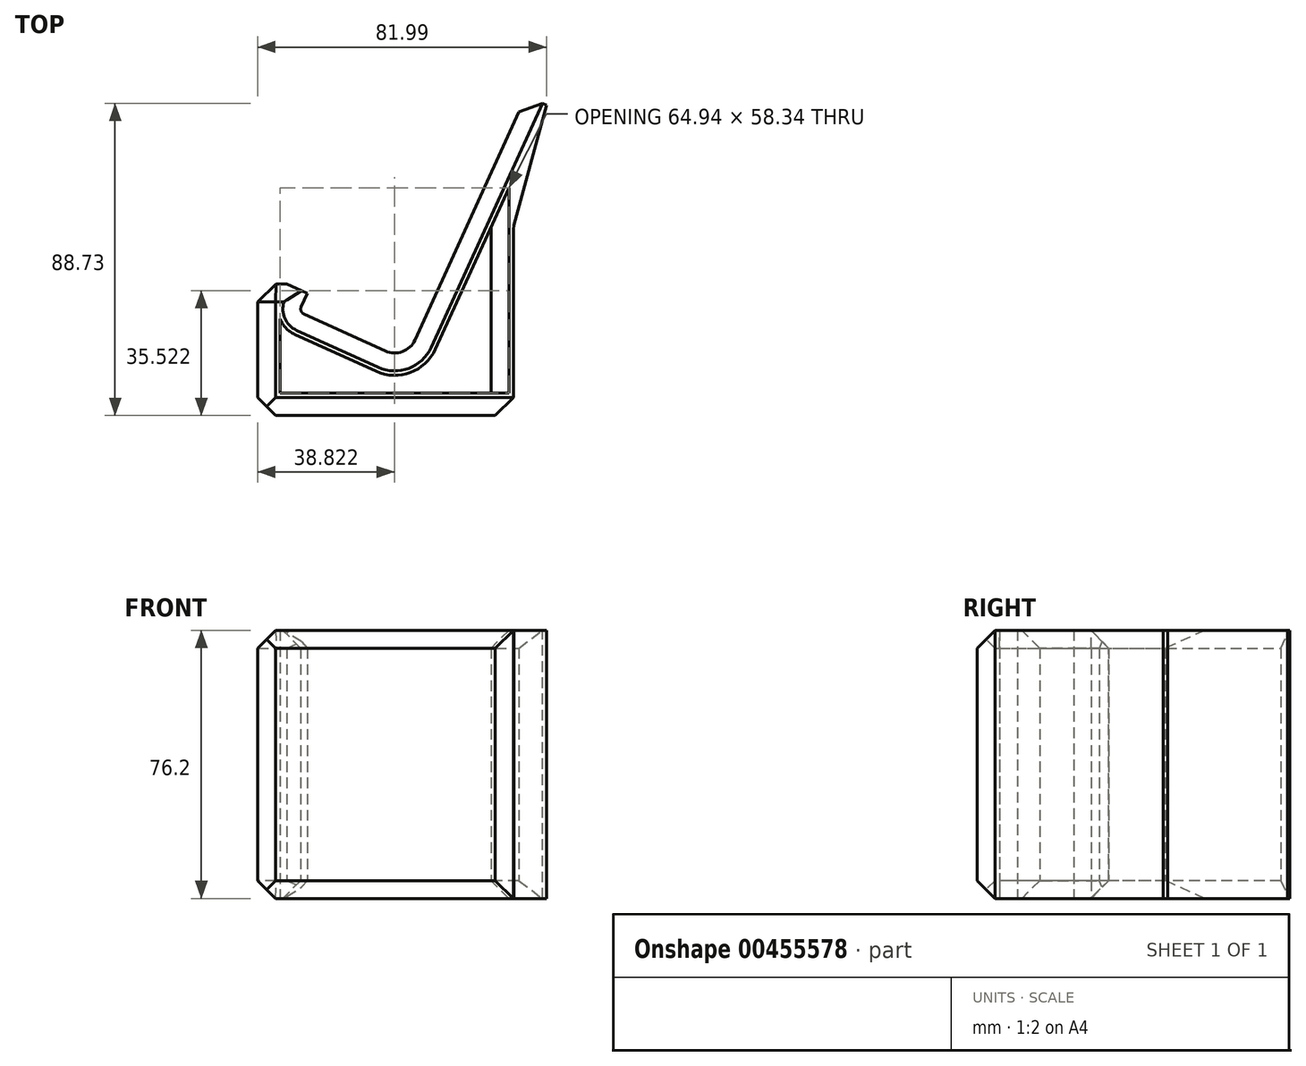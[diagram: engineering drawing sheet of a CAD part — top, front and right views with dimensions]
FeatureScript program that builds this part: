
annotation { "Feature Type Name" : "Feature", "Feature Type Description" : "" }
export const myFeature = defineFeature(function(context is Context, id is Id, definition is map)
    precondition{}
    {
        {
            var Q0;
            Q0=qCreatedBy(makeId("Top.planeOp"),FACE);
            var sketch = newSketch(context, id + "F0", { "sketchPlane" : qUnion([Q0])});
            skLineSegment(sketch, "E0", {"start": v(2.63, 5.78) * mm, "end": v(34.2, 75.14) * mm});
            skLineSegment(sketch, "E1", {"start": v(-5.78, 2.63) * mm, "end": v(-28.9, 13.15) * mm});
            skPoint(sketch, "E2.visualSharp", {"position": v(0, 0) * mm});
            skArc(sketch, "E2.filletArc", {"start": v(-5.78, 2.63) * mm, "mid": v(-0.92, 2.46) * mm, "end": v(2.63, 5.78) * mm});
            skLineSegment(sketch, "E3", {"start": v(-29.68, 15.24) * mm, "end": v(-27.95, 19.03) * mm});
            skPoint(sketch, "E4.visualSharp", {"position": v(-30.33, 13.8) * mm});
            skArc(sketch, "E4.filletArc", {"start": v(-29.68, 15.24) * mm, "mid": v(-29.72, 14.03) * mm, "end": v(-28.9, 13.15) * mm});
            skLineSegment(sketch, "E5.0", {"start": v(8.4, 3.15) * mm, "end": v(24.2, 37.83) * mm});
            skArc(sketch, "E5.2", {"start": v(-35.67, 11.8) * mm, "mid": v(-34.04, 9.18) * mm, "end": v(-31.53, 7.37) * mm});
            skLineSegment(sketch, "E5.3", {"start": v(-8.4, -3.15) * mm, "end": v(-31.53, 7.37) * mm});
            skArc(sketch, "E5.4", {"start": v(-8.4, -3.15) * mm, "mid": v(1.3, -3.48) * mm, "end": v(8.4, 3.15) * mm});
            skLineSegment(sketch, "E6", {"start": v(-33.73, 21.66) * mm, "end": v(-27.95, 19.03) * mm});
            skLineSegment(sketch, "E7", {"start": v(34.2, 75.14) * mm, "end": v(39.97, 72.5) * mm});
            skPoint(sketch, "E8", {"position": v(0, -9.35) * mm});
            skLineSegment(sketch, "E9", {"start": v(0, -9.35) * mm, "end": v(-35.67, -9.35) * mm});
            skPoint(sketch, "E9.endSnap0", {"position": v(-35.67, 11.8) * mm});
            skLineSegment(sketch, "E10", {"start": v(0, -9.35) * mm, "end": v(24.2, -9.35) * mm});
            skPoint(sketch, "E10.endSnap0", {"position": v(24.2, 37.83) * mm});
            skLineSegment(sketch, "E11", {"start": v(-35.67, 11.8) * mm, "end": v(-35.67, -9.35) * mm});
            skLineSegment(sketch, "E12", {"start": v(24.2, -9.35) * mm, "end": v(24.2, 37.83) * mm});
            skLineSegment(sketch, "E13.0", {"start": v(30.54, -15.7) * mm, "end": v(30.54, 37.83) * mm});
            skLineSegment(sketch, "E13.1", {"start": v(0, -15.7) * mm, "end": v(30.54, -15.7) * mm});
            skLineSegment(sketch, "E13.2", {"start": v(0, -15.7) * mm, "end": v(-42.02, -15.7) * mm});
            skLineSegment(sketch, "E13.3", {"start": v(-42.02, 11.8) * mm, "end": v(-42.02, -15.7) * mm});
            skLineSegment(sketch, "E14", {"start": v(30.54, 37.83) * mm, "end": v(39.97, 72.5) * mm});
            skLineSegment(sketch, "E15", {"start": v(-33.73, 21.66) * mm, "end": v(-42.02, 21.81) * mm});
            skLineSegment(sketch, "E16", {"start": v(-42.02, 21.81) * mm, "end": v(-42.02, 11.8) * mm});
            skSolve(sketch);
        }
        {
            var Q0;
            Q0=makeQuery(id+"F0.imprint","IMPRINT",FACE,{"disambiguationData":[TD([[makeQuery(id+"F0.imprint","IMPRINT",EDGE,{"derivedFrom":sQuery(id+"F0.wireOp",EDGE,"E0")}),-1.0]])]});
            extrude(context, id + "F1", {"entities" : qUnion([Q0]), "depth" : 76.2 * mm});
        }
        {
            var Q0;
            Q0=makeQuery(id+"F1.opExtrude","CAP_EDGE",EDGE,{"disambiguationData":[OSD([sQuery(id+"F0.wireOp",EDGE,"E13.3"),sQuery(id+"F0.wireOp",EDGE,"E16")])],"isStart":false});
            var Q1;
            Q1=makeQuery(id+"F1.opExtrude","CAP_EDGE",EDGE,{"disambiguationData":[OSD([sQuery(id+"F0.wireOp",EDGE,"E15")])],"isStart":false});
            var Q2;
            Q2=makeQuery(id+"F1.opExtrude","SWEPT_EDGE",EDGE,{"disambiguationData":[OSD([sQuery(id+"F0.wireOp",EDGE,"E15"),sQuery(id+"F0.wireOp",EDGE,"E16")])]});
            var Q3;
            Q3=makeQuery(id+"F1.opExtrude","CAP_EDGE",EDGE,{"disambiguationData":[OSD([sQuery(id+"F0.wireOp",EDGE,"E15")])],"isStart":true});
            var Q4;
            Q4=makeQuery(id+"F1.opExtrude","CAP_EDGE",EDGE,{"disambiguationData":[OSD([sQuery(id+"F0.wireOp",EDGE,"E3")])],"isStart":true});
            var Q5;
            Q5=makeQuery(id+"F1.opExtrude","CAP_EDGE",EDGE,{"disambiguationData":[OSD([sQuery(id+"F0.wireOp",EDGE,"E3")])],"isStart":false});
            var Q6;
            Q6=makeQuery(id+"F1.opExtrude","CAP_EDGE",EDGE,{"disambiguationData":[OSD([sQuery(id+"F0.wireOp",EDGE,"E13.3"),sQuery(id+"F0.wireOp",EDGE,"E16")])],"isStart":true});
            var Q7;
            Q7=makeQuery(id+"F1.opExtrude","SWEPT_EDGE",EDGE,{"disambiguationData":[OSD([sQuery(id+"F0.wireOp",EDGE,"E0"),sQuery(id+"F0.wireOp",EDGE,"E7")])]});
            chamfer(context, id + "F2", {"entities" : qUnion([Q0, Q1, Q2, Q3, Q4, Q5, Q6, Q7]), "width" : 5.08 * mm, "tangentPropagation" : true});
        }
        {
            var Q0;
            Q0=makeQuery(id+"F1.opExtrude","CAP_EDGE",EDGE,{"disambiguationData":[OSD([sQuery(id+"F0.wireOp",EDGE,"E13.1"),sQuery(id+"F0.wireOp",EDGE,"E13.2")])],"isStart":false});
            var Q1;
            Q1=makeQuery(id+"F1.opExtrude","CAP_EDGE",EDGE,{"disambiguationData":[OSD([sQuery(id+"F0.wireOp",EDGE,"E13.1"),sQuery(id+"F0.wireOp",EDGE,"E13.2")])],"isStart":true});
            var Q2;
            Q2=makeQuery(id+"F1.opExtrude","SWEPT_EDGE",EDGE,{"disambiguationData":[OSD([sQuery(id+"F0.wireOp",EDGE,"E13.2"),sQuery(id+"F0.wireOp",EDGE,"E13.3")])]});
            var Q3;
            Q3=makeQuery(id+"F1.opExtrude","SWEPT_EDGE",EDGE,{"disambiguationData":[OSD([sQuery(id+"F0.wireOp",EDGE,"E13.0"),sQuery(id+"F0.wireOp",EDGE,"E13.1")])]});
            var Q4;
            Q4=makeQuery(id+"F1.opExtrude","SWEPT_EDGE",EDGE,{"disambiguationData":[OSD([sQuery(id+"F0.wireOp",EDGE,"E13.0"),sQuery(id+"F0.wireOp",EDGE,"E14")])]});
            chamfer(context, id + "F3", {"entities" : qUnion([Q0, Q1, Q2, Q3, Q4]), "width" : 5.08 * mm, "tangentPropagation" : true});
        }
        {
            var Q0;
            Q0=makeQuery(id+"F1.opExtrude","CAP_EDGE",EDGE,{"disambiguationData":[OSD([sQuery(id+"F0.wireOp",EDGE,"E12")])],"isStart":true});
            var Q1;
            Q1=makeQuery(id+"F1.opExtrude","CAP_EDGE",EDGE,{"disambiguationData":[OSD([sQuery(id+"F0.wireOp",EDGE,"E12")])],"isStart":false});
            chamfer(context, id + "F4", {"entities" : qUnion([Q0, Q1]), "width" : 5.08 * mm, "tangentPropagation" : true});
        }
    });
